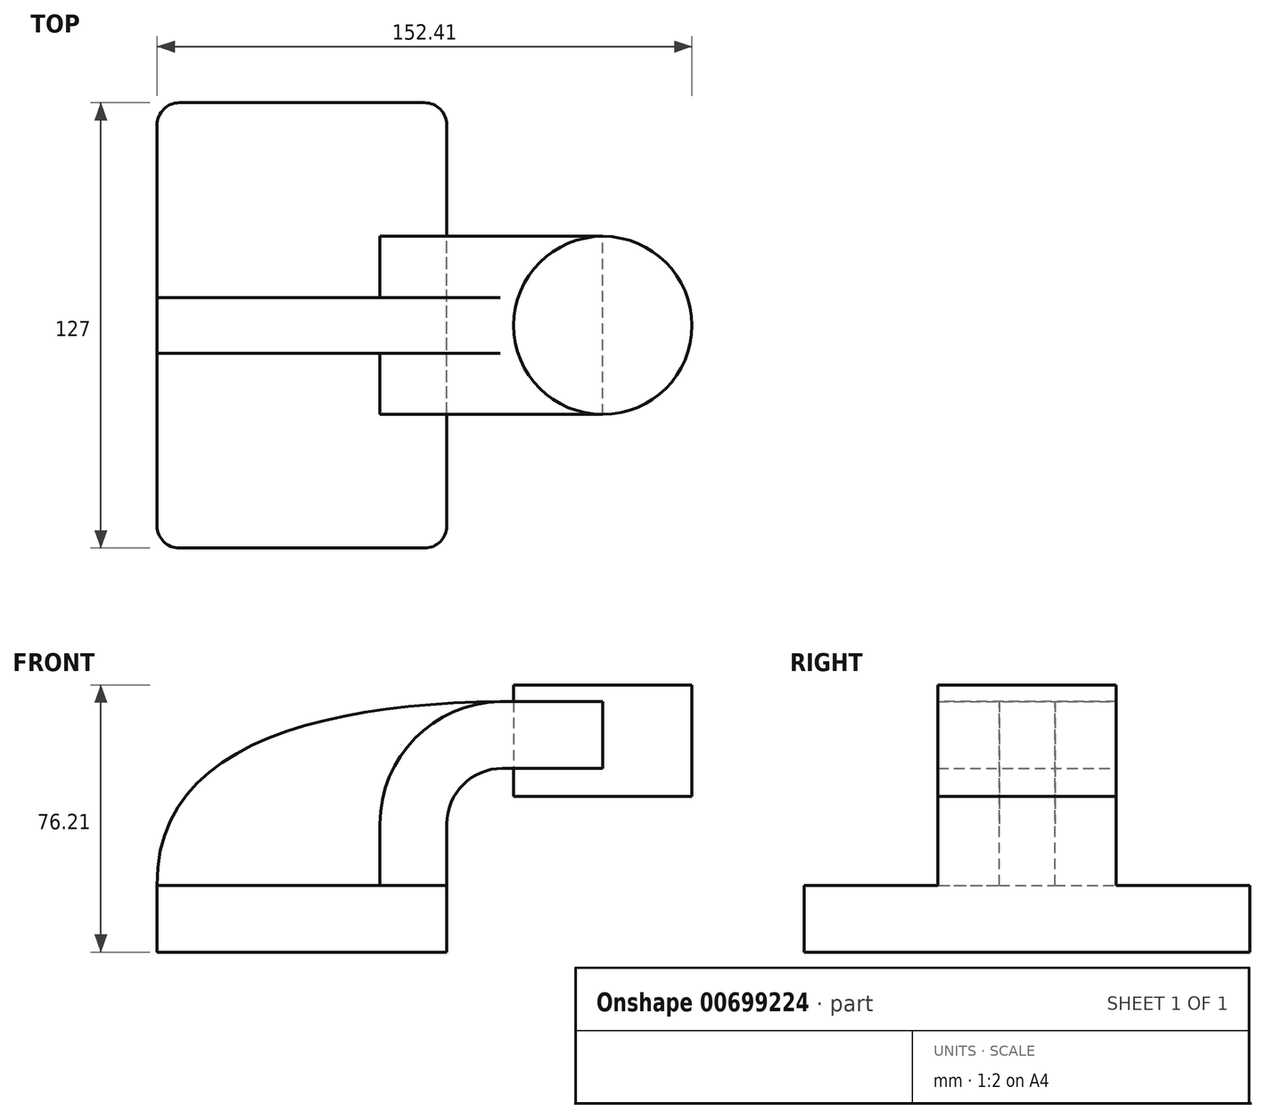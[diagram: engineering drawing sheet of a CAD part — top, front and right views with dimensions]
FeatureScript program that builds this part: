
annotation { "Feature Type Name" : "Feature", "Feature Type Description" : "" }
export const myFeature = defineFeature(function(context is Context, id is Id, definition is map)
    precondition{}
    {
        {
            var Q0;
            Q0=qCreatedBy(makeId("Front.planeOp"),FACE);
            var sketch = newSketch(context, id + "F0", { "sketchPlane" : qUnion([Q0])});
            skLineSegment(sketch, "E0.bottom", {"start": v(41.27, 9.53) * mm, "end": v(-41.28, 9.53) * mm});
            skLineSegment(sketch, "E0.top", {"start": v(41.28, -9.52) * mm, "end": v(-41.27, -9.52) * mm});
            skLineSegment(sketch, "E0.left", {"start": v(41.28, 9.53) * mm, "end": v(41.28, -9.52) * mm});
            skLineSegment(sketch, "E0.right", {"start": v(-41.28, 9.53) * mm, "end": v(-41.27, -9.52) * mm});
            skPoint(sketch, "E0.middle", {"position": v(0, 0) * mm});
            skLineSegment(sketch, "E1.bottom", {"start": v(111.12, 66.68) * mm, "end": v(60.32, 66.68) * mm});
            skLineSegment(sketch, "E1.top", {"start": v(111.12, 34.93) * mm, "end": v(60.32, 34.93) * mm});
            skLineSegment(sketch, "E1.left", {"start": v(111.12, 66.68) * mm, "end": v(111.12, 34.93) * mm});
            skLineSegment(sketch, "E1.right", {"start": v(60.32, 66.68) * mm, "end": v(60.32, 34.93) * mm});
            skPoint(sketch, "E1.middle", {"position": v(85.72, 50.8) * mm});
            skLineSegment(sketch, "E2", {"start": v(41.27, 9.53) * mm, "end": v(41.27, 27) * mm});
            skArc(sketch, "E3", {"start": v(41.27, 27) * mm, "mid": v(45.92, 38.23) * mm, "end": v(57.15, 42.88) * mm});
            skLineSegment(sketch, "E4", {"start": v(57.15, 42.88) * mm, "end": v(85.72, 42.88) * mm});
            skLineSegment(sketch, "E5.0", {"start": v(57.15, 61.93) * mm, "end": v(85.72, 61.93) * mm});
            skArc(sketch, "E5.1", {"start": v(22.23, 27) * mm, "mid": v(32.45, 51.7) * mm, "end": v(57.15, 61.93) * mm});
            skLineSegment(sketch, "E5.2", {"start": v(22.22, 9.53) * mm, "end": v(22.22, 27) * mm});
            skLineSegment(sketch, "E6", {"start": v(85.72, 34.93) * mm, "end": v(85.72, 66.68) * mm});
            skFitSpline(sketch, "E7", {"points": [v(-41.28, 9.52) * mm, v(57.15, 61.93) * mm], "startDerivative": vector(-1.8, 120.32) * mm, "endDerivative": vector(154.95, 1.35) * mm});
            skSolve(sketch);
        }
        {
            var Q0;
            Q0=makeQuery(id+"F0.imprint","IMPRINT",FACE,{"disambiguationData":[TD([[makeQuery(id+"F0.imprint","IMPRINT",EDGE,{"derivedFrom":sQuery(id+"F0.wireOp",EDGE,"E0.top")}),-1.0]])]});
            extrude(context, id + "F1", {"entities" : qUnion([Q0]), "depth" : 127 * mm, "offsetDistance" : 25.4 * mm, "symmetric" : true});
        }
        {
            var Q0;
            {var subQ1=sQuery(id+"F0.wireOp",EDGE,"E2");Q0=makeQuery(id+"F0.imprint","IMPRINT",FACE,{"disambiguationData":[TD([[makeQuery(id+"F0.imprint","IMPRINT",EDGE,{"derivedFrom":subQ1}),1.0]])]});}
            var Q1;
            {var subQ0=sQuery(id+"F0.wireOp",EDGE,"E5.0");var subQ1=sQuery(id+"F0.wireOp",EDGE,"E1.right");var subQ2=makeQuery(id+"F0.imprint","INTERSECT",VERTEX,{"derivedFrom":[subQ1,subQ0]});Q1=makeQuery(id+"F0.imprint","IMPRINT",FACE,{"disambiguationData":[TD([[makeQuery(id+"F0.imprint","IMPRINT",EDGE,{"disambiguationData":[TD([[subQ2,-1.0]])],"derivedFrom":subQ1}),1.0]])]});}
            extrude(context, id + "F2", {"entities" : qUnion([Q0, Q1]), "operationType" : NewBodyOperationType.ADD, "depth" : 50.8 * mm, "offsetDistance" : 25.4 * mm, "symmetric" : true});
        }
        {
            var Q0;
            {var subQ3=sQuery(id+"F0.wireOp",EDGE,"E5.2");Q0=makeQuery(id+"F0.imprint","IMPRINT",FACE,{"disambiguationData":[TD([[makeQuery(id+"F0.imprint","IMPRINT",EDGE,{"derivedFrom":subQ3}),1.0]])]});}
            extrude(context, id + "F3", {"entities" : qUnion([Q0]), "operationType" : NewBodyOperationType.ADD, "depth" : 15.88 * mm, "offsetDistance" : 25.4 * mm, "symmetric" : true});
        }
        {
            var Q0;
            {var subQ0=sQuery(id+"F0.wireOp",EDGE,"E1.left");Q0=makeQuery(id+"F0.imprint","IMPRINT",FACE,{"disambiguationData":[TD([[makeQuery(id+"F0.imprint","IMPRINT",EDGE,{"derivedFrom":subQ0}),-1.0]])]});}
            var Q1;
            Q1=sQuery(id+"F0.wireOp",EDGE,"E6");
            revolve(context, id + "F4", {"entities" : qUnion([Q0]), "axis" : qUnion([Q1]), "revolveType" : RevolveType.FULL});
        }
        {
            var Q0;
            Q0=makeQuery(id+"F1.opExtrude","CAP_EDGE",EDGE,{"disambiguationData":[OSD([sQuery(id+"F0.wireOp",EDGE,"E0.left")])],"isStart":false});
            var Q1;
            Q1=makeQuery(id+"F1.opExtrude","CAP_EDGE",EDGE,{"disambiguationData":[OSD([sQuery(id+"F0.wireOp",EDGE,"E0.right")])],"isStart":false});
            var Q2;
            Q2=makeQuery(id+"F1.opExtrude","CAP_EDGE",EDGE,{"disambiguationData":[OSD([sQuery(id+"F0.wireOp",EDGE,"E0.right")])],"isStart":true});
            var Q3;
            Q3=makeQuery(id+"F1.opExtrude","CAP_EDGE",EDGE,{"disambiguationData":[OSD([sQuery(id+"F0.wireOp",EDGE,"E0.left")])],"isStart":true});
            fillet(context, id + "F5", {"entities" : qUnion([Q0, Q1, Q2, Q3]), "radius" : 6.35 * mm, "tangentPropagation" : true, "allowEdgeOverflow" : false});
        }
    });
